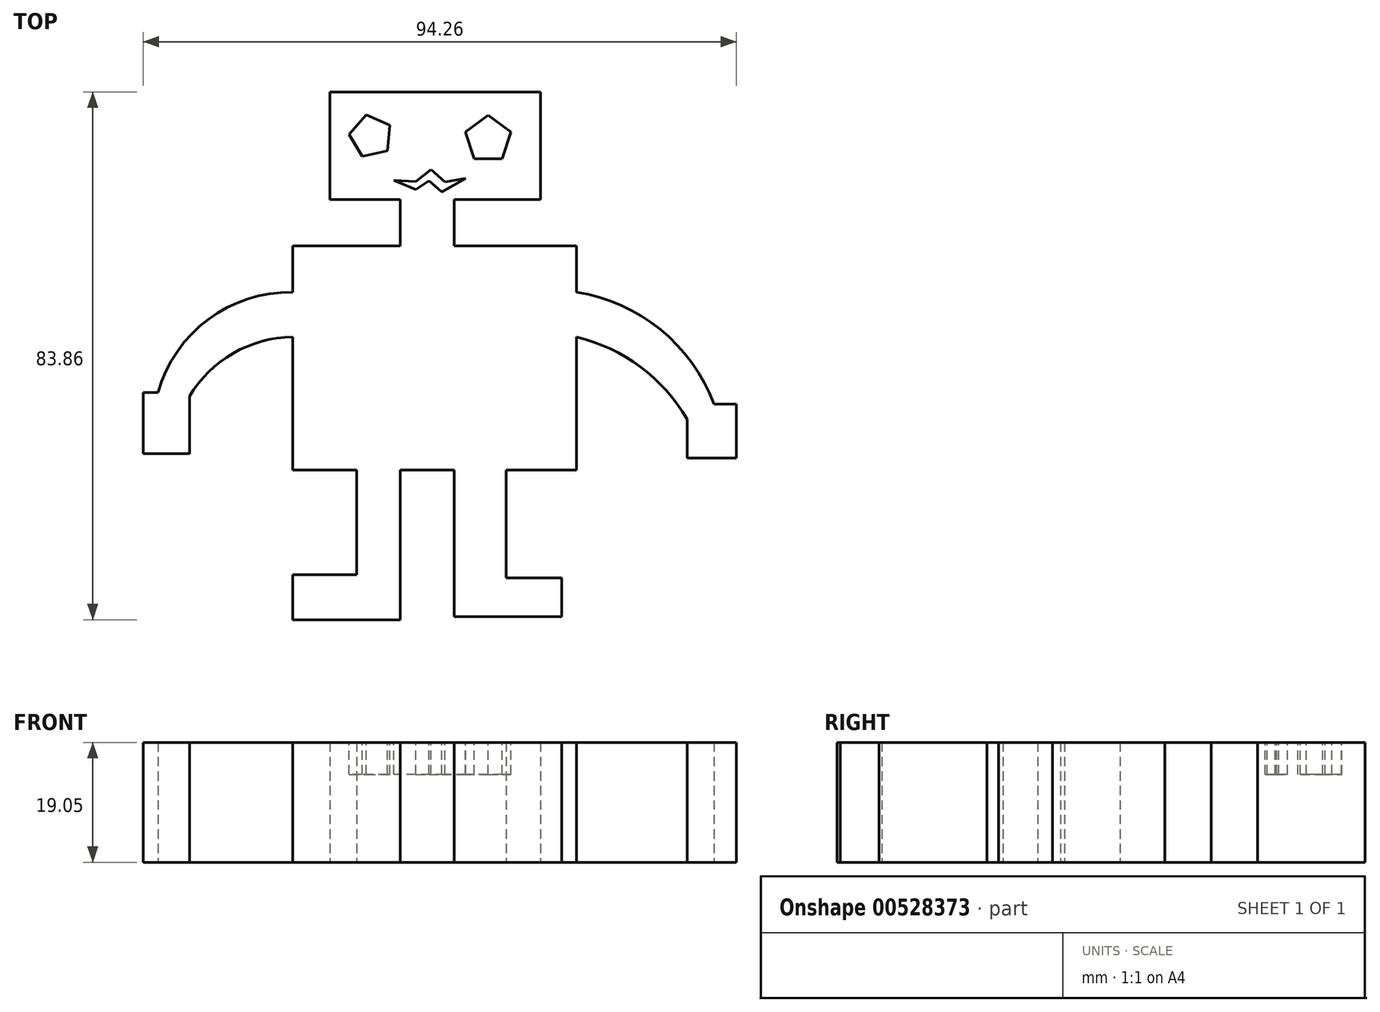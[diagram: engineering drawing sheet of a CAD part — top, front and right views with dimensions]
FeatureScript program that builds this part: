
annotation { "Feature Type Name" : "Feature", "Feature Type Description" : "" }
export const myFeature = defineFeature(function(context is Context, id is Id, definition is map)
    precondition{}
    {
        {
            var Q0;
            Q0=qCreatedBy(makeId("Top.planeOp"),FACE);
            var sketch = newSketch(context, id + "F0", { "sketchPlane" : qUnion([Q0])});
            skLineSegment(sketch, "E0.bottom", {"start": v(-15.2, 31.81) * mm, "end": v(18.28, 31.81) * mm});
            skLineSegment(sketch, "E0.top", {"start": v(-15.2, 14.72) * mm, "end": v(18.28, 14.72) * mm});
            skLineSegment(sketch, "E0.left", {"start": v(-15.2, 31.81) * mm, "end": v(-15.2, 14.72) * mm});
            skLineSegment(sketch, "E0.right", {"start": v(18.28, 31.81) * mm, "end": v(18.28, 14.72) * mm});
            skLineSegment(sketch, "E1", {"start": v(-4.04, 14.72) * mm, "end": v(-4.04, 7.36) * mm});
            skLineSegment(sketch, "E2", {"start": v(4.51, 14.72) * mm, "end": v(4.51, 7.36) * mm});
            skLineSegment(sketch, "E3.bottom", {"start": v(-21.13, 7.36) * mm, "end": v(23.98, 7.36) * mm});
            skLineSegment(sketch, "E3.top", {"start": v(-21.13, -28.25) * mm, "end": v(23.98, -28.25) * mm});
            skLineSegment(sketch, "E3.left", {"start": v(-21.13, 7.36) * mm, "end": v(-21.13, -28.25) * mm});
            skLineSegment(sketch, "E3.right", {"start": v(23.98, 7.36) * mm, "end": v(23.98, -28.25) * mm});
            skLineSegment(sketch, "E4.bottom", {"start": v(-10.93, -28.25) * mm, "end": v(-4.04, -28.25) * mm});
            skLineSegment(sketch, "E4.top", {"start": v(-10.93, -44.92) * mm, "end": v(-4.04, -44.92) * mm});
            skLineSegment(sketch, "E4.left", {"start": v(-10.93, -28.25) * mm, "end": v(-10.93, -44.92) * mm});
            skLineSegment(sketch, "E4.right", {"start": v(-4.04, -28.25) * mm, "end": v(-4.04, -44.92) * mm});
            skPoint(sketch, "E5.firstSnap0", {"position": v(1.42, -28.25) * mm});
            skLineSegment(sketch, "E5.bottom", {"start": v(4.51, -28.25) * mm, "end": v(12.8, -28.25) * mm});
            skLineSegment(sketch, "E5.top", {"start": v(4.51, -45.4) * mm, "end": v(12.8, -45.4) * mm});
            skLineSegment(sketch, "E5.left", {"start": v(4.51, -28.25) * mm, "end": v(4.51, -45.4) * mm});
            skLineSegment(sketch, "E5.right", {"start": v(12.8, -28.25) * mm, "end": v(12.8, -45.4) * mm});
            skLineSegment(sketch, "E6.bottom", {"start": v(4.51, -45.4) * mm, "end": v(21.6, -45.4) * mm});
            skLineSegment(sketch, "E6.top", {"start": v(4.51, -51.57) * mm, "end": v(21.6, -51.57) * mm});
            skLineSegment(sketch, "E6.left", {"start": v(4.51, -45.4) * mm, "end": v(4.51, -51.57) * mm});
            skLineSegment(sketch, "E6.right", {"start": v(21.6, -45.4) * mm, "end": v(21.6, -51.57) * mm});
            skLineSegment(sketch, "E7.bottom", {"start": v(-4.04, -44.92) * mm, "end": v(-21.13, -44.92) * mm});
            skLineSegment(sketch, "E7.top", {"start": v(-4.04, -52.05) * mm, "end": v(-21.13, -52.05) * mm});
            skLineSegment(sketch, "E7.left", {"start": v(-4.04, -44.92) * mm, "end": v(-4.04, -52.05) * mm});
            skLineSegment(sketch, "E7.right", {"start": v(-21.13, -44.92) * mm, "end": v(-21.13, -52.05) * mm});
            skArc(sketch, "E8", {"start": v(45.82, -17.82) * mm, "mid": v(37.32, -5.94) * mm, "end": v(23.98, 0) * mm});
            skArc(sketch, "E9", {"start": v(41.54, -20.2) * mm, "mid": v(34.1, -11.86) * mm, "end": v(23.98, -7.13) * mm});
            skArc(sketch, "E10", {"start": v(-21.13, 0) * mm, "mid": v(-34.53, -4.33) * mm, "end": v(-42.5, -15.94) * mm});
            skArc(sketch, "E11", {"start": v(-21.13, -7.13) * mm, "mid": v(-30.96, -9.94) * mm, "end": v(-38, -17.36) * mm});
            skLineSegment(sketch, "E12.bottom", {"start": v(-44.88, -15.94) * mm, "end": v(-37.52, -15.94) * mm});
            skLineSegment(sketch, "E12.top", {"start": v(-44.88, -25.68) * mm, "end": v(-37.52, -25.68) * mm});
            skLineSegment(sketch, "E12.left", {"start": v(-44.88, -15.94) * mm, "end": v(-44.88, -25.68) * mm});
            skLineSegment(sketch, "E12.right", {"start": v(-37.52, -15.94) * mm, "end": v(-37.52, -25.68) * mm});
            skLineSegment(sketch, "E13.bottom", {"start": v(49.38, -17.82) * mm, "end": v(41.54, -17.82) * mm});
            skLineSegment(sketch, "E13.top", {"start": v(49.38, -26.37) * mm, "end": v(41.54, -26.37) * mm});
            skLineSegment(sketch, "E13.left", {"start": v(49.38, -17.82) * mm, "end": v(49.38, -26.37) * mm});
            skLineSegment(sketch, "E13.right", {"start": v(41.54, -17.82) * mm, "end": v(41.54, -26.37) * mm});
            skSolve(sketch);
        }
        {
            var Q0;
            Q0 = qSketchRegion(id + "F0", true);
            extrude(context, id + "F1", {"entities" : qUnion([Q0]), "depth" : 19.05 * mm, "offsetDistance" : 25.4 * mm});
        }
        {
            var Q0;
            Q0=makeQuery(id+"F1.opExtrude","CAP_FACE",FACE,{"disambiguationData":[OSD([sQuery(id+"F0.wireOp",EDGE,"E0.bottom"),sQuery(id+"F0.wireOp",EDGE,"E0.top"),sQuery(id+"F0.wireOp",EDGE,"E0.left"),sQuery(id+"F0.wireOp",EDGE,"E0.right"),sQuery(id+"F0.wireOp",EDGE,"E1"),sQuery(id+"F0.wireOp",EDGE,"E2"),sQuery(id+"F0.wireOp",EDGE,"E3.bottom"),sQuery(id+"F0.wireOp",EDGE,"E3.top"),sQuery(id+"F0.wireOp",EDGE,"E3.left"),sQuery(id+"F0.wireOp",EDGE,"E3.right"),sQuery(id+"F0.wireOp",EDGE,"E4.left"),sQuery(id+"F0.wireOp",EDGE,"E4.right"),sQuery(id+"F0.wireOp",EDGE,"E5.left"),sQuery(id+"F0.wireOp",EDGE,"E5.right"),sQuery(id+"F0.wireOp",EDGE,"E6.bottom"),sQuery(id+"F0.wireOp",EDGE,"E6.top"),sQuery(id+"F0.wireOp",EDGE,"E6.left"),sQuery(id+"F0.wireOp",EDGE,"E6.right"),sQuery(id+"F0.wireOp",EDGE,"E7.bottom"),sQuery(id+"F0.wireOp",EDGE,"E7.top"),sQuery(id+"F0.wireOp",EDGE,"E7.left"),sQuery(id+"F0.wireOp",EDGE,"E7.right"),sQuery(id+"F0.wireOp",EDGE,"E8"),sQuery(id+"F0.wireOp",EDGE,"E9"),sQuery(id+"F0.wireOp",EDGE,"E10"),sQuery(id+"F0.wireOp",EDGE,"E11"),sQuery(id+"F0.wireOp",EDGE,"E12.bottom"),sQuery(id+"F0.wireOp",EDGE,"E12.top"),sQuery(id+"F0.wireOp",EDGE,"E12.left"),sQuery(id+"F0.wireOp",EDGE,"E12.right"),sQuery(id+"F0.wireOp",EDGE,"E13.bottom"),sQuery(id+"F0.wireOp",EDGE,"E13.top"),sQuery(id+"F0.wireOp",EDGE,"E13.left"),sQuery(id+"F0.wireOp",EDGE,"E13.right")])],"isStart":false});
            var sketch = newSketch(context, id + "F2", { "sketchPlane" : qUnion([Q0])});
            skCircle(sketch, "E14.cCircle", {"center": v(9.94, 24.27) * mm, "radius": 3.09 * mm, "construction": true});
            skLineSegment(sketch, "E14.0", {"start": v(12.18, 21.19) * mm, "end": v(7.7, 21.19) * mm});
            skLineSegment(sketch, "E14.1", {"start": v(7.7, 21.19) * mm, "end": v(6.3, 25.45) * mm});
            skLineSegment(sketch, "E14.2", {"start": v(6.3, 25.45) * mm, "end": v(9.94, 28.09) * mm});
            skLineSegment(sketch, "E14.3", {"start": v(9.94, 28.09) * mm, "end": v(13.57, 25.45) * mm});
            skLineSegment(sketch, "E14.4", {"start": v(13.57, 25.45) * mm, "end": v(12.18, 21.19) * mm});
            skPoint(sketch, "E14.0.midPoint", {"position": v(9.94, 21.19) * mm});
            skCircle(sketch, "E15.cCircle", {"center": v(-8.68, 24.77) * mm, "radius": 2.82 * mm, "construction": true});
            skLineSegment(sketch, "E15.0", {"start": v(-6.05, 22.48) * mm, "end": v(-10.05, 21.57) * mm});
            skLineSegment(sketch, "E15.1", {"start": v(-10.05, 21.57) * mm, "end": v(-12.15, 25.09) * mm});
            skLineSegment(sketch, "E15.2", {"start": v(-12.15, 25.09) * mm, "end": v(-9.45, 28.17) * mm});
            skLineSegment(sketch, "E15.3", {"start": v(-9.45, 28.17) * mm, "end": v(-5.69, 26.56) * mm});
            skLineSegment(sketch, "E15.4", {"start": v(-5.69, 26.56) * mm, "end": v(-6.05, 22.48) * mm});
            skPoint(sketch, "E15.0.midPoint", {"position": v(-8.05, 22.02) * mm});
            skLineSegment(sketch, "E16", {"start": v(-5.04, 17.79) * mm, "end": v(-1.54, 16.29) * mm});
            skLineSegment(sketch, "E17", {"start": v(-1.54, 16.29) * mm, "end": v(0.55, 17.69) * mm});
            skLineSegment(sketch, "E18", {"start": v(0.55, 17.69) * mm, "end": v(2.55, 15.94) * mm});
            skLineSegment(sketch, "E19", {"start": v(2.55, 15.94) * mm, "end": v(6.4, 18.09) * mm});
            skLineSegment(sketch, "E20", {"start": v(6.4, 18.09) * mm, "end": v(3.05, 17.54) * mm});
            skLineSegment(sketch, "E21", {"start": v(3.05, 17.54) * mm, "end": v(0.83, 19.48) * mm});
            skLineSegment(sketch, "E22", {"start": v(0.83, 19.48) * mm, "end": v(-1.54, 17.59) * mm});
            skLineSegment(sketch, "E23", {"start": v(-1.54, 17.59) * mm, "end": v(-5.04, 17.79) * mm});
            skSolve(sketch);
        }
        {
            var Q0;
            Q0 = qSketchRegion(id + "F2", true);
            extrude(context, id + "F3", {"entities" : qUnion([Q0]), "operationType" : NewBodyOperationType.REMOVE, "oppositeDirection" : true, "depth" : 5.08 * mm, "offsetDistance" : 25.4 * mm});
        }
    });
